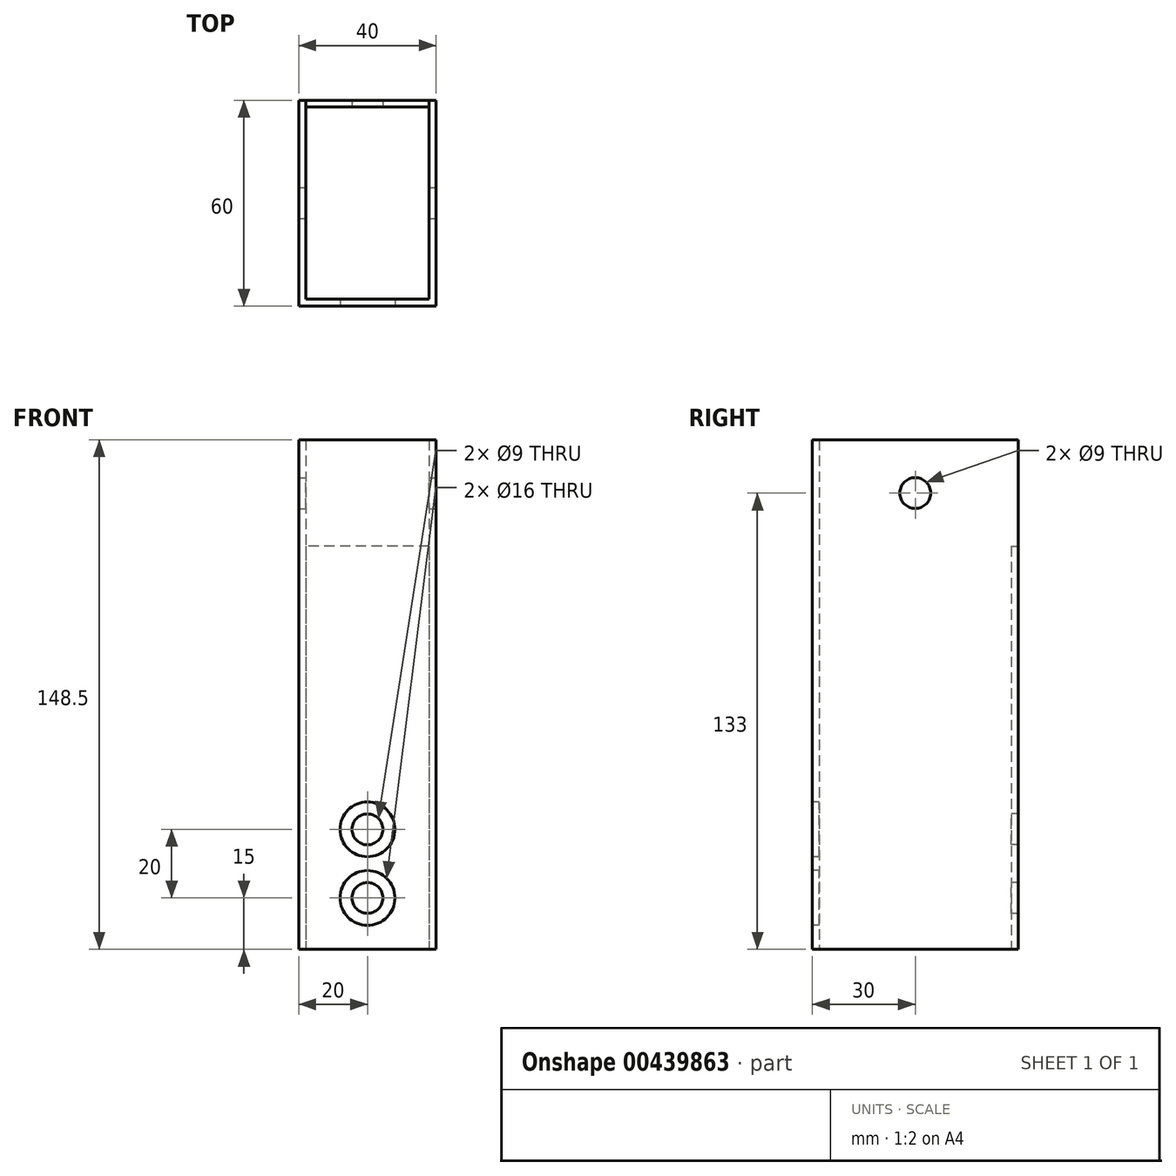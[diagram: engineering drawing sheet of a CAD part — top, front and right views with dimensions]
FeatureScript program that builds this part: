
annotation { "Feature Type Name" : "Feature", "Feature Type Description" : "" }
export const myFeature = defineFeature(function(context is Context, id is Id, definition is map)
    precondition{}
    {
        {
            assignVariable(context, id + "F0", {"name" : "x1", "anyValue" : 2});
        }
        {
            assignVariable(context, id + "F1", {"name" : "x3", "anyValue" : 31});
        }
        {
            var Q0;
            Q0=qCreatedBy(makeId("Top.planeOp"),FACE);
            var sketch = newSketch(context, id + "F2", { "sketchPlane" : qUnion([Q0])});
            skLineSegment(sketch, "E0.bottom", {"start": v(0, 0) * mm, "end": v(-40, 0) * mm});
            skLineSegment(sketch, "E0.top", {"start": v(0, -60) * mm, "end": v(-40, -60) * mm});
            skLineSegment(sketch, "E0.left", {"start": v(0, 0) * mm, "end": v(0, -60) * mm});
            skLineSegment(sketch, "E0.right", {"start": v(-40, 0) * mm, "end": v(-40, -60) * mm});
            skSolve(sketch);
        }
        {
            var Q0;
            Q0=makeQuery(id+"F2.imprint","IMPRINT",FACE,{"disambiguationData":[TD([[makeQuery(id+"F2.imprint","IMPRINT",EDGE,{"derivedFrom":sQuery(id+"F2.wireOp",EDGE,"E0.bottom")}),1.0]])]});
            extrude(context, id + "F3", {"entities" : qUnion([Q0]), "depth" : (117.5 + getVariable(context, 'x3')) * mm});
        }
        {
            var Q0;
            Q0=makeQuery(id+"F3.opExtrude","CAP_FACE",FACE,{"disambiguationData":[OSD([sQuery(id+"F2.wireOp",EDGE,"E0.bottom"),sQuery(id+"F2.wireOp",EDGE,"E0.top"),sQuery(id+"F2.wireOp",EDGE,"E0.left"),sQuery(id+"F2.wireOp",EDGE,"E0.right"),sQuery(id+"F2.wireOp",EDGE,"DtiuugUZ-L0Yc-QAZo-6dP0-kDZpmOFYKq8W.left")])],"isStart":false});
            var Q1;
            Q1=makeQuery(id+"F3.opExtrude","CAP_FACE",FACE,{"disambiguationData":[OSD([sQuery(id+"F2.wireOp",EDGE,"E0.bottom"),sQuery(id+"F2.wireOp",EDGE,"E0.top"),sQuery(id+"F2.wireOp",EDGE,"E0.left"),sQuery(id+"F2.wireOp",EDGE,"E0.right"),sQuery(id+"F2.wireOp",EDGE,"DtiuugUZ-L0Yc-QAZo-6dP0-kDZpmOFYKq8W.left")])],"isStart":true});
            shell(context, id + "F4", {"entities" : qUnion([Q0, Q1]), "thickness" : (getVariable(context, 'x1')) * mm});
        }
        {
            var Q0;
            Q0=makeQuery(id+"F3.opExtrude","SWEPT_FACE",FACE,{"disambiguationData":[OSD([sQuery(id+"F2.wireOp",EDGE,"E0.bottom")])]});
            var sketch = newSketch(context, id + "F5", { "sketchPlane" : qUnion([Q0])});
            skLineSegment(sketch, "E1.bottom", {"start": v(2, 148.5) * mm, "end": v(38, 148.5) * mm});
            skLineSegment(sketch, "E1.top", {"start": v(2, 117.5) * mm, "end": v(38, 117.5) * mm});
            skLineSegment(sketch, "E1.left", {"start": v(2, 148.5) * mm, "end": v(2, 117.5) * mm});
            skLineSegment(sketch, "E1.right", {"start": v(38, 148.5) * mm, "end": v(38, 117.5) * mm});
            skSolve(sketch);
        }
        {
            var Q0;
            Q0=qSketchRegion(id+"F5",true);
            extrude(context, id + "F6", {"entities" : qUnion([Q0]), "operationType" : NewBodyOperationType.REMOVE, "endBound" : BoundingType.UP_TO_NEXT, "oppositeDirection" : true, "depth" : 25 * mm});
        }
        {
            var Q0;
            Q0=qCreatedBy(makeId("Right.planeOp"),FACE);
            var sketch = newSketch(context, id + "F7", { "sketchPlane" : qUnion([Q0])});
            skLineSegment(sketch, "E2.0.0", {"start": v(-60, 0) * mm, "end": v(0, 0) * mm});
            skLineSegment(sketch, "E2.0.1", {"start": v(0, 0) * mm, "end": v(0, 148.5) * mm});
            skLineSegment(sketch, "E2.0.2", {"start": v(0, 148.5) * mm, "end": v(-60, 148.5) * mm});
            skLineSegment(sketch, "E2.0.3", {"start": v(-60, 148.5) * mm, "end": v(-60, 0) * mm});
            skCircle(sketch, "E3", {"center": v(-30, 133) * mm, "radius": 4.5 * mm});
            skSolve(sketch);
        }
        {
            var Q0;
            Q0=makeQuery(id+"F7.imprint","IMPRINT",FACE,{"disambiguationData":[TD([[makeQuery(id+"F7.imprint","IMPRINT",EDGE,{"derivedFrom":sQuery(id+"F7.wireOp",EDGE,"E3")}),1.0]])]});
            extrude(context, id + "F8", {"entities" : qUnion([Q0]), "operationType" : NewBodyOperationType.REMOVE, "endBound" : BoundingType.THROUGH_ALL, "oppositeDirection" : true, "depth" : 25 * mm});
        }
        {
            var Q0;
            Q0=makeQuery(id+"F3.opExtrude","SWEPT_FACE",FACE,{"disambiguationData":[OSD([sQuery(id+"F2.wireOp",EDGE,"E0.top")])]});
            var sketch = newSketch(context, id + "F9", { "sketchPlane" : qUnion([Q0])});
            skCircle(sketch, "E4", {"center": v(-20, 15) * mm, "radius": 4.5 * mm});
            skCircle(sketch, "E5", {"center": v(-20, 35) * mm, "radius": 4.5 * mm});
            skCircle(sketch, "E6", {"center": v(-20, 35) * mm, "radius": 8 * mm});
            skCircle(sketch, "E7", {"center": v(-20, 15) * mm, "radius": 8 * mm});
            skSolve(sketch);
        }
        {
            var Q0;
            Q0=makeQuery(id+"F9.imprint","IMPRINT",FACE,{"disambiguationData":[TD([[makeQuery(id+"F9.imprint","IMPRINT",EDGE,{"derivedFrom":sQuery(id+"F9.wireOp",EDGE,"E5")}),1.0]])]});
            var Q1;
            Q1=makeQuery(id+"F9.imprint","IMPRINT",FACE,{"disambiguationData":[TD([[makeQuery(id+"F9.imprint","IMPRINT",EDGE,{"derivedFrom":sQuery(id+"F9.wireOp",EDGE,"E4")}),1.0]])]});
            extrude(context, id + "F10", {"entities" : qUnion([Q0, Q1]), "operationType" : NewBodyOperationType.REMOVE, "endBound" : BoundingType.THROUGH_ALL, "oppositeDirection" : true, "depth" : 25 * mm});
        }
        {
            var Q0;
            Q0=makeQuery(id+"F9.imprint","IMPRINT",FACE,{"disambiguationData":[TD([[makeQuery(id+"F9.imprint","IMPRINT",EDGE,{"derivedFrom":sQuery(id+"F9.wireOp",EDGE,"E5")}),-1.0]])]});
            var Q1;
            Q1=makeQuery(id+"F9.imprint","IMPRINT",FACE,{"disambiguationData":[TD([[makeQuery(id+"F9.imprint","IMPRINT",EDGE,{"derivedFrom":sQuery(id+"F9.wireOp",EDGE,"E4")}),-1.0]])]});
            extrude(context, id + "F11", {"entities" : qUnion([Q0, Q1]), "operationType" : NewBodyOperationType.REMOVE, "endBound" : BoundingType.UP_TO_NEXT, "oppositeDirection" : true, "depth" : 25 * mm});
        }
    });
